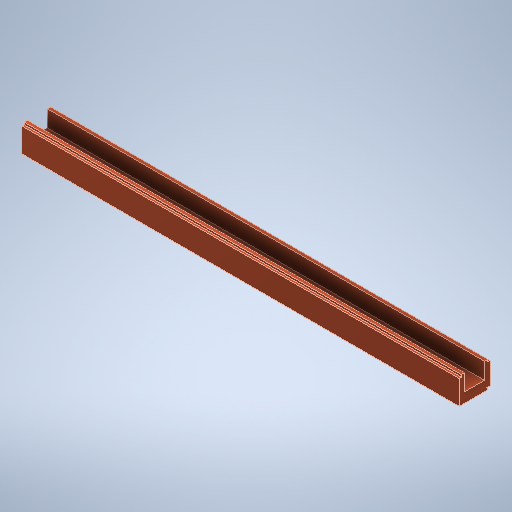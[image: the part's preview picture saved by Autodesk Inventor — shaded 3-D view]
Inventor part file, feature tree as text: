
AUTODESK INVENTOR PART (.ipt)
format: ipt  version: 2025.1 (Build 291241000, 241)  size: 300,544 bytes
history: native  units: mm
features: extrude x2, sketch x2, fillet x1
ambient origin geometry x8: Origin, YZ Plane, XZ Plane, XY Plane, X Axis, Y Axis, Z Axis, Center Point
bodies: Solid1 (feature_tree)
feature tree (5):
  extrude  "Extrusion1"  Depth=90.0mm
  extrude  "Extrusion2"  Depth=10.0mm
  fillet  "Fillet2"  Radius=35.0mm
  sketch  "Sketch1"  dims[d10=1985.0mm d11=0.0mm d15=90.0mm]
  sketch  "Sketch2"  dims[d16=110.0mm d17=10.0mm d20=35.0mm d21=15.0mm d22=15.0mm d23=15.0mm d24=10.0mm d25=10.0mm d26=135.0deg d27=135.0deg d28=90.0mm d32=10.0mm d33=0.0mm d36=10.0mm d43=15.0mm d44=5.0mm]
